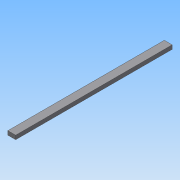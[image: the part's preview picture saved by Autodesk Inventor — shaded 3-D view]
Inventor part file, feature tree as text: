
AUTODESK INVENTOR PART (.ipt)
format: ipt  version: 2015 (Build 190159000, 159)  size: 68,096 bytes
history: native  units: mm
features: extrude x1, sketch x1
ambient origin geometry x8: Origin, YZ Plane, XZ Plane, XY Plane, X Axis, Y Axis, Z Axis, Center Point
bodies: Solid1 (feature_tree)
feature tree (2):
  extrude  "Extrusion1"  Depth=5.0mm
  sketch  "Sketch1"  dims[d0=10.0mm d1=5.0mm d2=200.0mm d3=0.0mm]
